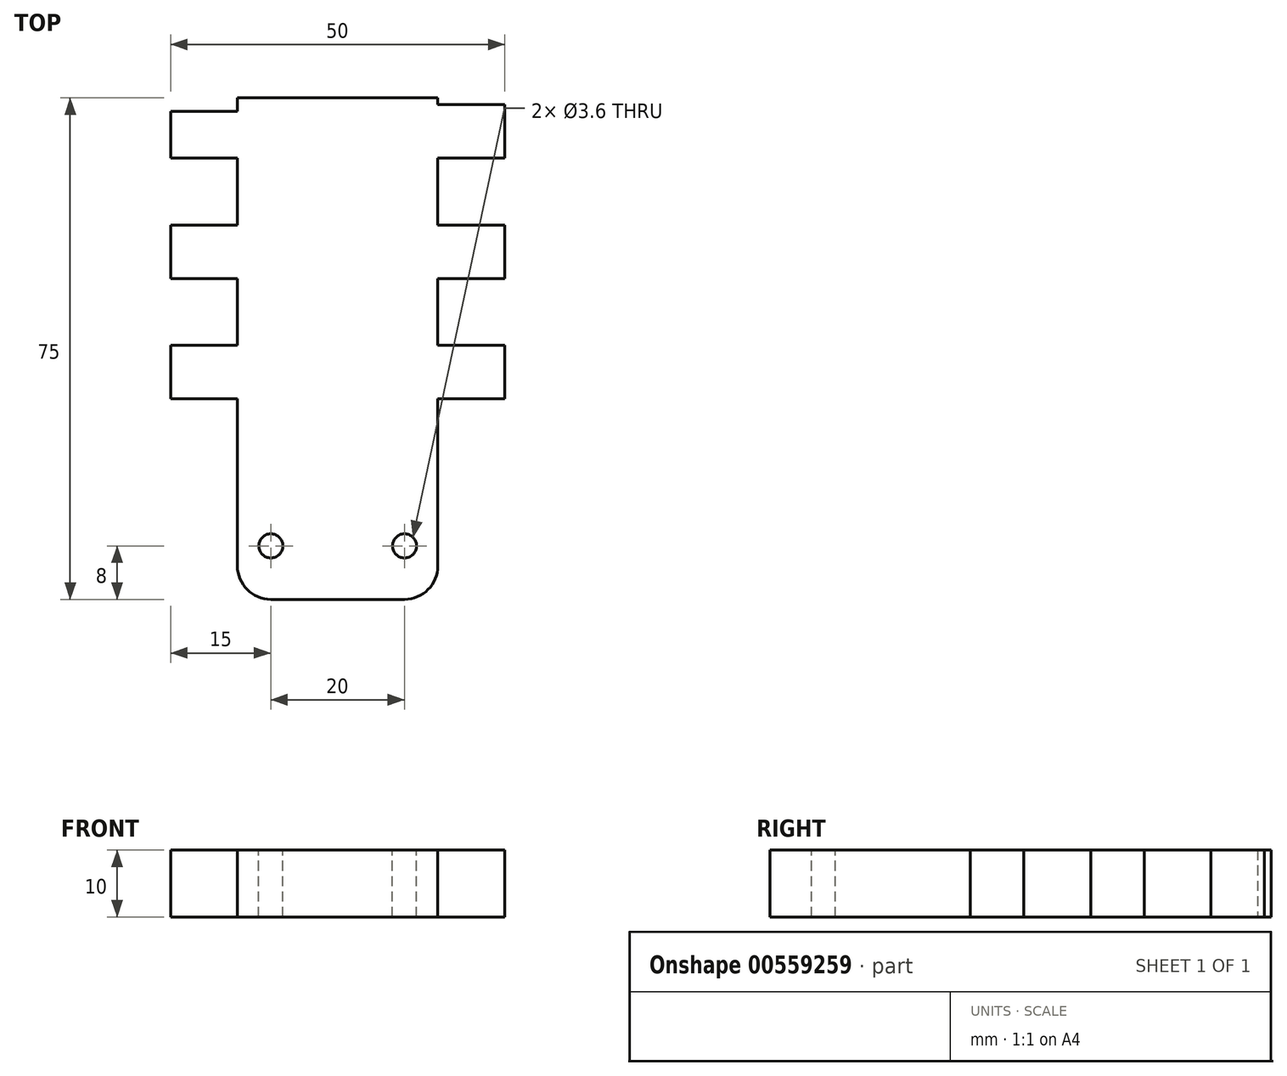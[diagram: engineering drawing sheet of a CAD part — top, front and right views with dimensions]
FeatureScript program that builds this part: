
annotation { "Feature Type Name" : "Feature", "Feature Type Description" : "" }
export const myFeature = defineFeature(function(context is Context, id is Id, definition is map)
    precondition{}
    {
        {
            var Q0;
            Q0=qCreatedBy(makeId("Top.planeOp"),FACE);
            var sketch = newSketch(context, id + "F0", { "sketchPlane" : qUnion([Q0])});
            skLineSegment(sketch, "E0.bottom", {"start": v(15, 37.5) * mm, "end": v(-15, 37.5) * mm});
            skLineSegment(sketch, "E0.top", {"start": v(15, -37.5) * mm, "end": v(-15, -37.5) * mm});
            skLineSegment(sketch, "E0.left", {"start": v(15, 37.5) * mm, "end": v(15, -37.5) * mm});
            skLineSegment(sketch, "E0.right", {"start": v(-15, 37.5) * mm, "end": v(-15, -37.5) * mm});
            skPoint(sketch, "E0.middle", {"position": v(0, 0) * mm});
            skLineSegment(sketch, "E1.bottom", {"start": v(-15, -7.5) * mm, "end": v(-25, -7.5) * mm});
            skLineSegment(sketch, "E1.top", {"start": v(-15, 0.5) * mm, "end": v(-25, 0.5) * mm});
            skLineSegment(sketch, "E1.left", {"start": v(-15, -7.5) * mm, "end": v(-15, 0.5) * mm});
            skLineSegment(sketch, "E1.right", {"start": v(-25, -7.5) * mm, "end": v(-25, 0.5) * mm});
            skLineSegment(sketch, "E2.bottom", {"start": v(15, -7.5) * mm, "end": v(25, -7.5) * mm});
            skLineSegment(sketch, "E2.top", {"start": v(15, 0.5) * mm, "end": v(25, 0.5) * mm});
            skLineSegment(sketch, "E2.left", {"start": v(15, -7.5) * mm, "end": v(15, 0.5) * mm});
            skLineSegment(sketch, "E2.right", {"start": v(25, -7.5) * mm, "end": v(25, 0.5) * mm});
            skLineSegment(sketch, "E3.bottom", {"start": v(-15, 10.5) * mm, "end": v(-25, 10.5) * mm});
            skLineSegment(sketch, "E3.top", {"start": v(-15, 18.5) * mm, "end": v(-25, 18.5) * mm});
            skLineSegment(sketch, "E3.left", {"start": v(-15, 10.5) * mm, "end": v(-15, 18.5) * mm});
            skLineSegment(sketch, "E3.right", {"start": v(-25, 10.5) * mm, "end": v(-25, 18.5) * mm});
            skLineSegment(sketch, "E4.bottom", {"start": v(15, 10.5) * mm, "end": v(25, 10.5) * mm});
            skLineSegment(sketch, "E4.top", {"start": v(15, 18.5) * mm, "end": v(25, 18.5) * mm});
            skLineSegment(sketch, "E4.left", {"start": v(15, 10.5) * mm, "end": v(15, 18.5) * mm});
            skLineSegment(sketch, "E4.right", {"start": v(25, 10.5) * mm, "end": v(25, 18.5) * mm});
            skLineSegment(sketch, "E5.bottom", {"start": v(-15, 28.5) * mm, "end": v(-25, 28.5) * mm});
            skLineSegment(sketch, "E5.top", {"start": v(-15, 35.5) * mm, "end": v(-25, 35.5) * mm});
            skLineSegment(sketch, "E5.left", {"start": v(-15, 28.5) * mm, "end": v(-15, 35.5) * mm});
            skLineSegment(sketch, "E5.right", {"start": v(-25, 28.5) * mm, "end": v(-25, 35.5) * mm});
            skLineSegment(sketch, "E6.bottom", {"start": v(15, 28.5) * mm, "end": v(25, 28.5) * mm});
            skLineSegment(sketch, "E6.top", {"start": v(15, 36.5) * mm, "end": v(25, 36.5) * mm});
            skLineSegment(sketch, "E6.left", {"start": v(15, 28.5) * mm, "end": v(15, 36.5) * mm});
            skLineSegment(sketch, "E6.right", {"start": v(25, 28.5) * mm, "end": v(25, 36.5) * mm});
            skSolve(sketch);
        }
        {
            var Q0;
            Q0=qSketchRegion(id+"F0",true);
            extrude(context, id + "F1", {"entities" : qUnion([Q0]), "depth" : 10 * mm, "offsetDistance" : 25 * mm});
        }
        {
            var Q0;
            Q0=makeQuery(id+"F1.opExtrude","CAP_FACE",FACE,{"disambiguationData":[OSD([sQuery(id+"F0.wireOp",EDGE,"E0.bottom"),sQuery(id+"F0.wireOp",EDGE,"E0.top"),sQuery(id+"F0.wireOp",EDGE,"E0.left"),sQuery(id+"F0.wireOp",EDGE,"E0.right")])],"isStart":false});
            var sketch = newSketch(context, id + "F2", { "sketchPlane" : qUnion([Q0])});
            skCircle(sketch, "E7", {"center": v(-10, -29.5) * mm, "radius": 1.8 * mm});
            skCircle(sketch, "E8", {"center": v(10, -29.5) * mm, "radius": 1.8 * mm});
            skSolve(sketch);
        }
        {
            var Q0;
            Q0=qSketchRegion(id+"F2",true);
            extrude(context, id + "F3", {"entities" : qUnion([Q0]), "operationType" : NewBodyOperationType.REMOVE, "oppositeDirection" : true, "depth" : 10 * mm, "offsetDistance" : 25 * mm});
        }
        {
            var Q0;
            Q0=makeQuery(id+"F1.opExtrude","SWEPT_EDGE",EDGE,{"disambiguationData":[OSD([sQuery(id+"F0.wireOp",EDGE,"E0.top"),sQuery(id+"F0.wireOp",EDGE,"E0.left")])]});
            var Q1;
            Q1=makeQuery(id+"F1.opExtrude","SWEPT_EDGE",EDGE,{"disambiguationData":[OSD([sQuery(id+"F0.wireOp",EDGE,"E0.top"),sQuery(id+"F0.wireOp",EDGE,"E0.right")])]});
            fillet(context, id + "F4", {"entities" : qUnion([Q0, Q1]), "radius" : 5 * mm, "tangentPropagation" : true, "allowEdgeOverflow" : false});
        }
    });
